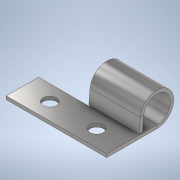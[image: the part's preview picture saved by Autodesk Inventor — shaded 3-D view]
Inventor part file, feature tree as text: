
AUTODESK INVENTOR PART (.ipt)
format: ipt  version: 2022 (Build 260153000, 153)  size: 159,744 bytes
history: native  units: mm
features: other x8, sketch x5, hole x1
ambient origin geometry x8: Origin, YZ Plane, XZ Plane, XY Plane, X Axis, Y Axis, Z Axis, Center Point
bodies: Body1 (feature_tree)
feature tree (14):
  other  "Sólido1"
  other  "Flange de contorno1"
  other  "Borda1"
  hole  "Furo1"  [1 undecoded]
  sketch  "Esboço1"  dims[d0=15.0mm d1=0.5mm]
  other  "Placa1"
  other  "Vergadura1"
  other  "Canto1"
  sketch  "Esboço2"  dims[d2=0.5mm]
  sketch  "Esboço4"  dims[d4=1.0mm]
  sketch  "Esboço5"  dims[d5=0.5mm d6=10.0mm d7=0.5mm d8=0.5mm d9=2.0mm d10=0.5mm d11=0.5mm d12=5.0mm d13=0.5mm d14=0.0mm d15=0.5mm d16=0.25mm d17=1.0mm d18=0.5mm d19=46.251225mm d20=2.0mm d21=2.0mm d22=2.0mm d23=6.0mm d24=4.0mm d25=2.0mm d26=90.0deg d27=0.5mm d28=20.594885mm d29=0.5mm d30=0.0mm]
  other  "Recortar1"
  other  "Recortar2"
  sketch  "Esboço3"  dims[d3=0.25mm]
note: 1 required parameter value undecoded (feature->parameter linkage not recoverable at this tier; creation-order binding heuristic only, values carry confidence <= 0.55)
